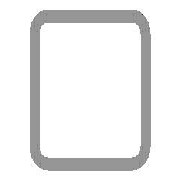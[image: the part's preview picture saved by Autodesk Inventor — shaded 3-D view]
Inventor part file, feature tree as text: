
AUTODESK INVENTOR PART (.ipt)
format: ipt  version: 2022 (Build 260153000, 153)  size: 143,360 bytes
history: native  units: mm (DEFAULTED — no unit token found)
features: other x4, sketch x3, plane x2, split x1
ambient origin geometry x8: Origin, YZ Plane, XZ Plane, XY Plane, X Axis, Y Axis, Z Axis, Center Point
bodies: Solid1 (feature_tree), Body (feature_tree)
feature tree (10):
  parser-record x1  (decoder bookkeeping rows leaked as tree rows — omitted from the tree; the rows remain in map.json)
  other  "Driven Length"
  other  "Start Plane"
  other  "End Plane"
  plane  "Work Plane4"
  split  "Split1"
  sketch  "Sketch"  dims[d7=8.0mm d9=40.0mm d11=40.0mm d12=4.0mm d13=-0.0mm d14=118.284271mm d15=20.0mm d16=20.0mm d17=90.0deg d18=118.284271mm]
  sketch  "Sketch3"  dims[d3=118.284271mm]
  plane  "Work Plane3"
  sketch  "Sketch4"  dims[d4=0.0mm]
